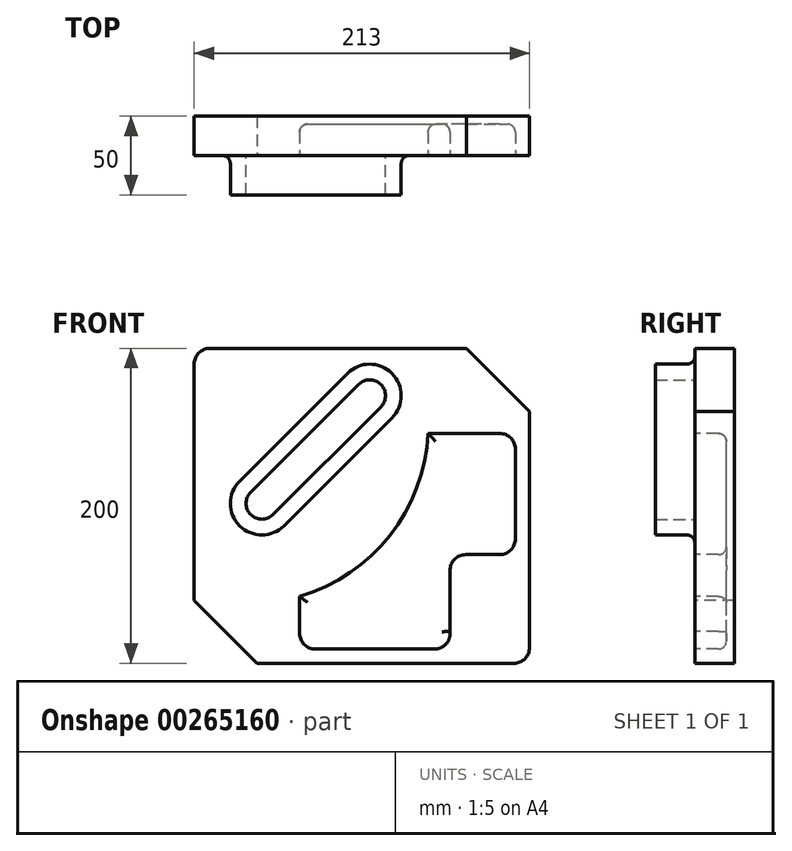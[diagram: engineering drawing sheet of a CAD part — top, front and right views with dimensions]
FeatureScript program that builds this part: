
annotation { "Feature Type Name" : "Feature", "Feature Type Description" : "" }
export const myFeature = defineFeature(function(context is Context, id is Id, definition is map)
    precondition{}
    {
        {
            var Q0;
            Q0=qCreatedBy(makeId("Front.planeOp"),FACE);
            var sketch = newSketch(context, id + "F0", { "sketchPlane" : qUnion([Q0])});
            skLineSegment(sketch, "E0", {"start": v(0, 0) * mm, "end": v(-40, 40) * mm});
            skLineSegment(sketch, "E1", {"start": v(-40, 40) * mm, "end": v(-40, 190) * mm});
            skArc(sketch, "E2", {"start": v(-30, 200) * mm, "mid": v(-37.07, 197.07) * mm, "end": v(-40, 190) * mm});
            skLineSegment(sketch, "E3", {"start": v(-30, 200) * mm, "end": v(133, 200) * mm});
            skLineSegment(sketch, "E4", {"start": v(133, 200) * mm, "end": v(173, 160) * mm});
            skLineSegment(sketch, "E5", {"start": v(173, 160) * mm, "end": v(173, 10) * mm});
            skArc(sketch, "E6", {"start": v(163, 0) * mm, "mid": v(170.07, 2.93) * mm, "end": v(173, 10) * mm});
            skLineSegment(sketch, "E7", {"start": v(0, 0) * mm, "end": v(163, 0) * mm});
            skLineSegment(sketch, "E8", {"start": v(71.5, 200) * mm, "end": v(71.5, 90.81) * mm, "construction": true});
            skLineSegment(sketch, "E9", {"start": v(-40, 101.5) * mm, "end": v(47.05, 101.5) * mm, "construction": true});
            skLineSegment(sketch, "E10", {"start": v(3, 171.44) * mm, "end": v(3, -15.96) * mm, "construction": true});
            skLineSegment(sketch, "E11", {"start": v(0, 170) * mm, "end": v(191.48, 170) * mm, "construction": true});
            skArc(sketch, "E12", {"start": v(78.57, 162.93) * mm, "mid": v(78.57, 177.07) * mm, "end": v(64.43, 177.07) * mm});
            skArc(sketch, "E13", {"start": v(52.18, 164.82) * mm, "mid": v(57.36, 155.86) * mm, "end": v(66.32, 150.68) * mm});
            skArc(sketch, "E14", {"start": v(-4.07, 108.57) * mm, "mid": v(-4.07, 94.43) * mm, "end": v(10.07, 94.43) * mm});
            skArc(sketch, "E15", {"start": v(-11.14, 115.64) * mm, "mid": v(-11.14, 87.36) * mm, "end": v(17.14, 87.36) * mm});
            skLineSegment(sketch, "E16", {"start": v(-11.14, 115.64) * mm, "end": v(57.36, 184.14) * mm});
            skLineSegment(sketch, "E17", {"start": v(17.14, 87.36) * mm, "end": v(85.64, 155.86) * mm});
            skLineSegment(sketch, "E18", {"start": v(-4.07, 108.57) * mm, "end": v(64.43, 177.07) * mm});
            skLineSegment(sketch, "E19", {"start": v(10.07, 94.43) * mm, "end": v(78.57, 162.93) * mm});
            skArc(sketch, "E20.trimOffspring", {"start": v(85.64, 155.86) * mm, "mid": v(85.64, 184.14) * mm, "end": v(57.36, 184.14) * mm});
            skLineSegment(sketch, "E21", {"start": v(37, 9) * mm, "end": v(112.59, 9) * mm});
            skArc(sketch, "E22", {"start": v(112.59, 9) * mm, "mid": v(120.13, 12.44) * mm, "end": v(122.49, 20.4) * mm});
            skLineSegment(sketch, "E23", {"start": v(132.49, 69) * mm, "end": v(154, 69) * mm});
            skArc(sketch, "E24", {"start": v(154, 69) * mm, "mid": v(161.07, 71.93) * mm, "end": v(164, 79) * mm});
            skLineSegment(sketch, "E25", {"start": v(164, 79) * mm, "end": v(164, 136) * mm});
            skLineSegment(sketch, "E26", {"start": v(154, 146) * mm, "end": v(108.63, 146) * mm});
            skArc(sketch, "E27", {"start": v(27, 19) * mm, "mid": v(29.93, 11.93) * mm, "end": v(37, 9) * mm});
            skLineSegment(sketch, "E28", {"start": v(27, 19) * mm, "end": v(27, 42.42) * mm});
            skArc(sketch, "E29", {"start": v(164, 136) * mm, "mid": v(161.07, 143.07) * mm, "end": v(154, 146) * mm});
            skLineSegment(sketch, "E30", {"start": v(-4.07, 94.43) * mm, "end": v(78.57, 177.07) * mm, "construction": true});
            skArc(sketch, "E31", {"start": v(27, 42.42) * mm, "mid": v(84.31, 81.2) * mm, "end": v(108.63, 146) * mm});
            skLineSegment(sketch, "E32", {"start": v(122.49, 20.4) * mm, "end": v(122.49, 59) * mm});
            skArc(sketch, "E33", {"start": v(132.49, 69) * mm, "mid": v(125.42, 66.07) * mm, "end": v(122.49, 59) * mm});
            skSolve(sketch);
        }
        {
            var Q0;
            Q0=makeQuery(id+"F0.imprint","IMPRINT",FACE,{"disambiguationData":[TD([[makeQuery(id+"F0.imprint","IMPRINT",EDGE,{"derivedFrom":sQuery(id+"F0.wireOp",EDGE,"E0")}),-1.0]])]});
            var Q1;
            Q1=makeQuery(id+"F0.imprint","IMPRINT",FACE,{"disambiguationData":[TD([[makeQuery(id+"F0.imprint","IMPRINT",EDGE,{"derivedFrom":sQuery(id+"F0.wireOp",EDGE,"E21")}),1.0]])]});
            var Q2;
            {var subQ4=sQuery(id+"F0.wireOp",EDGE,"E12");Q2=makeQuery(id+"F0.imprint","IMPRINT",FACE,{"disambiguationData":[TD([[makeQuery(id+"F0.imprint","IMPRINT",EDGE,{"derivedFrom":subQ4}),-1.0]])]});}
            var Q3;
            {var subQ0=sQuery(id+"F0.wireOp",EDGE,"E13");Q3=makeQuery(id+"F0.imprint","IMPRINT",FACE,{"disambiguationData":[TD([[makeQuery(id+"F0.imprint","IMPRINT",EDGE,{"derivedFrom":subQ0}),-1.0]])]});}
            var Q4;
            {var subQ0=sQuery(id+"F0.wireOp",EDGE,"E12");Q4=makeQuery(id+"F0.imprint","IMPRINT",FACE,{"disambiguationData":[TD([[makeQuery(id+"F0.imprint","IMPRINT",EDGE,{"derivedFrom":subQ0}),1.0]])]});}
            extrude(context, id + "F1", {"entities" : qUnion([Q0, Q1, Q2, Q3, Q4]), "oppositeDirection" : true, "depth" : 25 * mm});
        }
        {
            var Q0;
            {var subQ4=sQuery(id+"F0.wireOp",EDGE,"E12");Q0=makeQuery(id+"F0.imprint","IMPRINT",FACE,{"disambiguationData":[TD([[makeQuery(id+"F0.imprint","IMPRINT",EDGE,{"derivedFrom":subQ4}),-1.0]])]});}
            extrude(context, id + "F2", {"entities" : qUnion([Q0]), "operationType" : NewBodyOperationType.ADD, "depth" : 25 * mm});
        }
        {
            var Q0;
            Q0=makeQuery(id+"F0.imprint","IMPRINT",FACE,{"disambiguationData":[TD([[makeQuery(id+"F0.imprint","IMPRINT",EDGE,{"derivedFrom":sQuery(id+"F0.wireOp",EDGE,"E21")}),1.0]])]});
            extrude(context, id + "F3", {"entities" : qUnion([Q0]), "operationType" : NewBodyOperationType.REMOVE, "oppositeDirection" : true, "depth" : 20 * mm});
        }
        {
            var Q0;
            Q0=makeQuery(id+"F2.opExtrude","CAP_EDGE",EDGE,{"disambiguationData":[OSD([sQuery(id+"F0.wireOp",EDGE,"E17")])],"isStart":true});
            var Q1;
            Q1=makeQuery(id+"F3.boolean.opBoolean","COPY",EDGE,{"derivedFrom":makeQuery(id+"F3.opExtrude","CAP_EDGE",EDGE,{"disambiguationData":[OSD([sQuery(id+"F0.wireOp",EDGE,"E31")])],"isStart":true})});
            var Q2;
            Q2=makeQuery(id+"F3.boolean.opBoolean","COPY",EDGE,{"derivedFrom":makeQuery(id+"F3.opExtrude","CAP_EDGE",EDGE,{"disambiguationData":[OSD([sQuery(id+"F0.wireOp",EDGE,"E31")])],"isStart":false})});
            var Q3;
            Q3=makeQuery(id+"F3.boolean.opBoolean","COPY",EDGE,{"derivedFrom":makeQuery(id+"F3.opExtrude","CAP_EDGE",EDGE,{"disambiguationData":[OSD([sQuery(id+"F0.wireOp",EDGE,"E26")])],"isStart":false})});
            var Q4;
            Q4=makeQuery(id+"F3.boolean.opBoolean","COPY",EDGE,{"derivedFrom":makeQuery(id+"F3.opExtrude","CAP_EDGE",EDGE,{"disambiguationData":[OSD([sQuery(id+"F0.wireOp",EDGE,"E26")])],"isStart":true})});
            var Q5;
            Q5=makeQuery(id+"F3.boolean.opBoolean","COPY",EDGE,{"derivedFrom":makeQuery(id+"F3.opExtrude","CAP_EDGE",EDGE,{"disambiguationData":[OSD([sQuery(id+"F0.wireOp",EDGE,"E28")])],"isStart":true})});
            var Q6;
            Q6=makeQuery(id+"F3.boolean.opBoolean","COPY",EDGE,{"derivedFrom":makeQuery(id+"F3.opExtrude","CAP_EDGE",EDGE,{"disambiguationData":[OSD([sQuery(id+"F0.wireOp",EDGE,"E28")])],"isStart":false})});
            fillet(context, id + "F4", {"entities" : qUnion([Q0, Q1, Q2, Q3, Q4, Q5, Q6]), "radius" : 5 * mm, "tangentPropagation" : true, "allowEdgeOverflow" : false});
        }
    });
